# Revit family: Mixer-Kitchen-GBG-Nautic_GB41206056
name_source: partatom
category: Plumbing Fixtures
revit_build: Autodesk Revit 2017 (Build: 20190508_0315(x64)
units: mm (PartAtom-declared; Revit-internal decimal feet)

## family parameters
Always vertical = No
Cut with Voids When Loaded = No
OmniClass Number = 23.45.55.00
OmniClass Title = Sanitary Faucets, Wastes
Part Type = Normal
Room Calculation Point = No
Round Connector Dimension = Use Radius
Shared = No
Work Plane-Based = Yes

## types (3) — shared parameters
Assembly Code = D2010
Care Instruction URL = http://www.gustavsberg.com
Code NRF NOR = -
Connector Description = Ø10
Default Elevation = 900 mm
Description = Kitchen mixer, high Spout, Energy class B
Height = 370 mm
Installation Instruction URL = https://www.gustavsberg.com
Length = 215 mm
Manufacturer = Villeroy & Boch Gustavsberg
Material = Metal - Gustavsberg - Polished Chrome
Nominal Flow = 0.1 L/s
Pressure Drop = 300.0 kPa
Product Family = Nautic
Product Page URL = https://www.gustavsberg.com
URL = http://www.gustavsberg.com
Vent Connection = No
Waste Connection = No

## per-type parameters (varying)
| type | Article Number | Code EAN | Code LVI FIN | Code RSK SWE | Code VVS DNK | Cold Water Connection Diameter | Cold Water Connection Radius | Hot Water Connection Diameter | Hot Water Connection Radius | Model |
| Ø10, chrome | GB41206056 | 7393792235464 | 6270859 | 8311481 | 706029204 | 10 mm  [stored 0.0328084 ft] | 5 mm  [stored 0.0164042 ft] | 10 mm  [stored 0.0328084 ft] | 5 mm  [stored 0.0164042 ft] | GB41206056 |
| Ø10, Lead free, chrome | GB412060560 | 7393792235457 | 6270871 | 8311472 | 706029304 | 10 mm  [stored 0.0328084 ft] | 5 mm  [stored 0.0164042 ft] | 10 mm  [stored 0.0328084 ft] | 5 mm  [stored 0.0164042 ft] | GB412060560 |
| G3/8, chrome | GB41206056R | 7393792235471 | 6270864 | 8311483 | 706029234 | 15 mm | 8 mm  [stored 0.0262467 ft] | 15 mm | 8 mm  [stored 0.0262467 ft] | GB41206056R |

note: column(s) folded — value = type name in every type: Type Comments

note: [stored X ft] marks values corroborated as IEEE doubles in the binary element streams (Revit-internal decimal feet)

## geometry (parser evidence)
native form markers: Sweep x6
no freeform markers — native parametric forms only
